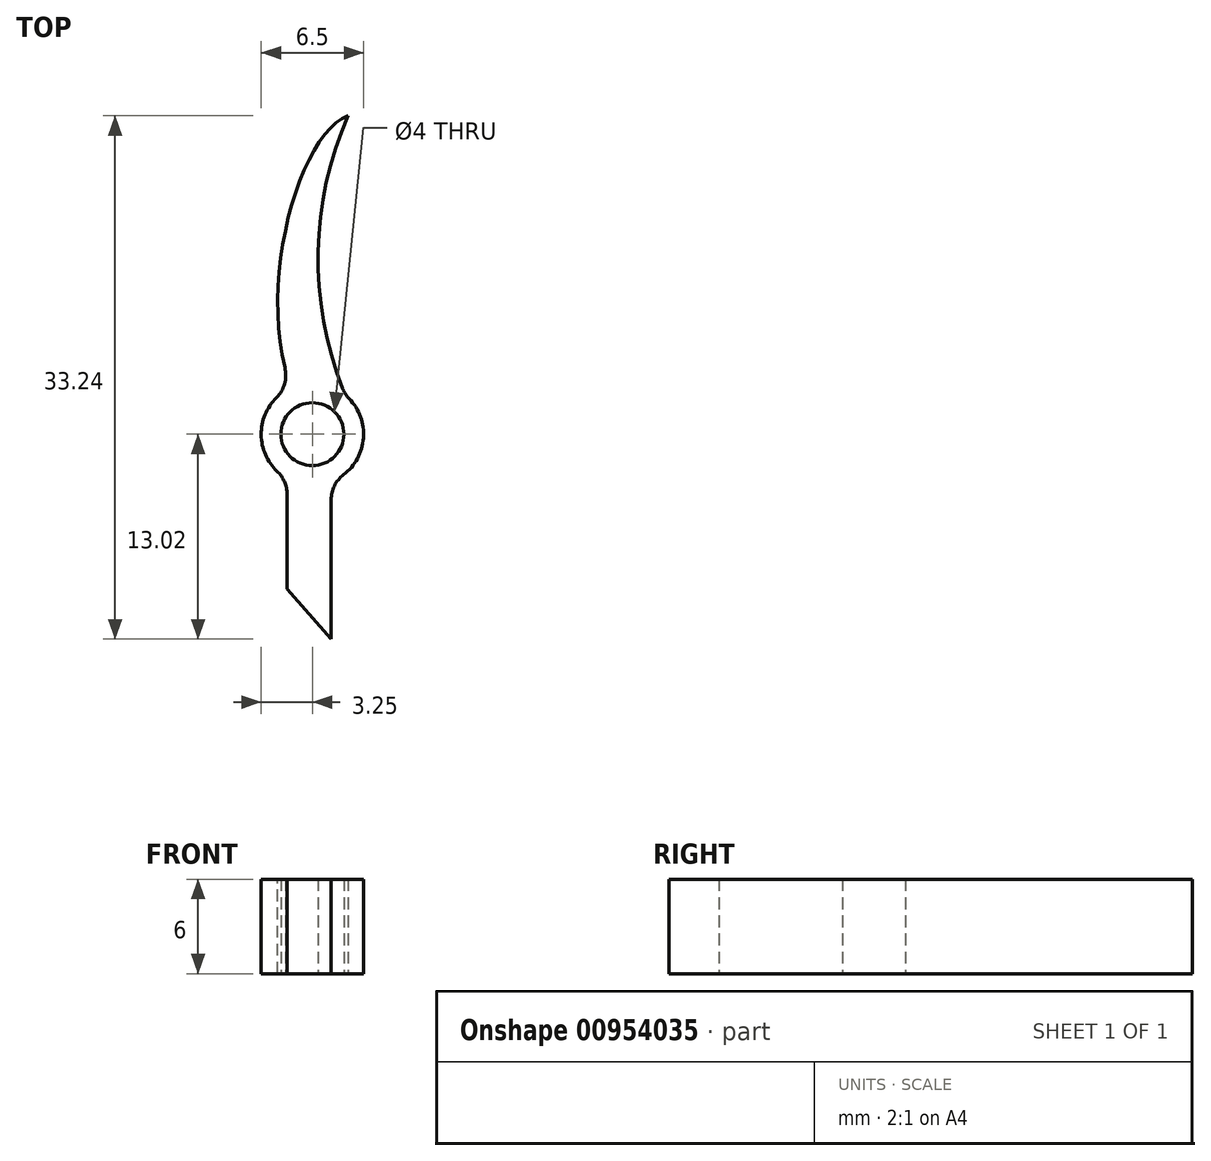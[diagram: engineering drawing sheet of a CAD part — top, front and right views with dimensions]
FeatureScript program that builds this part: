
annotation { "Feature Type Name" : "Feature", "Feature Type Description" : "" }
export const myFeature = defineFeature(function(context is Context, id is Id, definition is map)
    precondition{}
    {
        {
            var Q0;
            Q0=qCreatedBy(makeId("Top.planeOp"),FACE);
            var sketch = newSketch(context, id + "F0", { "sketchPlane" : qUnion([Q0])});
            skCircle(sketch, "E0", {"center": v(0, 0) * mm, "radius": 2 * mm});
            skCircle(sketch, "E1", {"center": v(0, 0) * mm, "radius": 3.25 * mm});
            skLineSegment(sketch, "E2", {"start": v(-1.61, -2.82) * mm, "end": v(-1.61, -9.82) * mm});
            skLineSegment(sketch, "E3.MirrorCS", {"start": v(1.2, -3.02) * mm, "end": v(1.2, -13.02) * mm});
            skLineSegment(sketch, "E4", {"start": v(-1.61, -9.82) * mm, "end": v(1.2, -13.02) * mm});
            skFitSpline(sketch, "E5", {"points": [v(-1.36, 2.95) * mm, v(2.28, 20.22) * mm], "startDerivative": vector(-6.87, 18.58) * mm, "endDerivative": vector(9.53, 3.39) * mm});
            skArc(sketch, "E6", {"start": v(2.28, 20.22) * mm, "mid": v(0.36, 11.37) * mm, "end": v(2.1, 2.48) * mm});
            skSolve(sketch);
        }
        {
            var Q0;
            Q0=makeQuery(id+"F0.imprint","IMPRINT",FACE,{"disambiguationData":[TD([[makeQuery(id+"F0.imprint","IMPRINT",EDGE,{"derivedFrom":sQuery(id+"F0.wireOp",EDGE,"E0")}),-1.0]])]});
            var Q1;
            {var subQ0=sQuery(id+"F0.wireOp",EDGE,"E2");Q1=makeQuery(id+"F0.imprint","IMPRINT",FACE,{"disambiguationData":[TD([[makeQuery(id+"F0.imprint","IMPRINT",EDGE,{"derivedFrom":subQ0}),1.0]])]});}
            var Q2;
            {var subQ0=sQuery(id+"F0.wireOp",EDGE,"8be97a24-eb7d-44bc-b59b-ebb2be015d9e");Q2=makeQuery(id+"F0.imprint","IMPRINT",FACE,{"disambiguationData":[TD([[makeQuery(id+"F0.imprint","IMPRINT",EDGE,{"derivedFrom":subQ0}),-1.0]])]});}
            var Q3;
            {var subQ0=sQuery(id+"F0.wireOp",EDGE,"E5");Q3=makeQuery(id+"F0.imprint","IMPRINT",FACE,{"disambiguationData":[TD([[makeQuery(id+"F0.imprint","IMPRINT",EDGE,{"derivedFrom":subQ0}),-1.0]])]});}
            extrude(context, id + "F1", {"entities" : qUnion([Q0, Q1, Q2, Q3]), "depth" : 6 * mm, "offsetDistance" : 25 * mm});
        }
        {
            var Q0;
            Q0=makeQuery(id+"F1.opExtrude","SWEPT_EDGE",EDGE,{"disambiguationData":[OSD([sQuery(id+"F0.wireOp",EDGE,"E1"),sQuery(id+"F0.wireOp",EDGE,"E2")])]});
            var Q1;
            Q1=makeQuery(id+"F1.opExtrude","SWEPT_EDGE",EDGE,{"disambiguationData":[OSD([sQuery(id+"F0.wireOp",EDGE,"E1"),sQuery(id+"F0.wireOp",EDGE,"E3.MirrorCS")])]});
            var Q2;
            Q2=makeQuery(id+"F1.opExtrude","SWEPT_EDGE",EDGE,{"disambiguationData":[OSD([sQuery(id+"F0.wireOp",EDGE,"E1"),sQuery(id+"F0.wireOp",EDGE,"WLQRXf7D-uZFB-bk0P-7e7V-tLiNUVGfqJje")])]});
            var Q3;
            Q3=makeQuery(id+"F1.opExtrude","SWEPT_EDGE",EDGE,{"disambiguationData":[OSD([sQuery(id+"F0.wireOp",EDGE,"E1"),sQuery(id+"F0.wireOp",EDGE,"8be97a24-eb7d-44bc-b59b-ebb2be015d9e")])]});
            fillet(context, id + "F2", {"entities" : qUnion([Q0, Q1, Q2, Q3]), "radius" : 2 * mm, "tangentPropagation" : true, "allowEdgeOverflow" : false});
        }
    });
